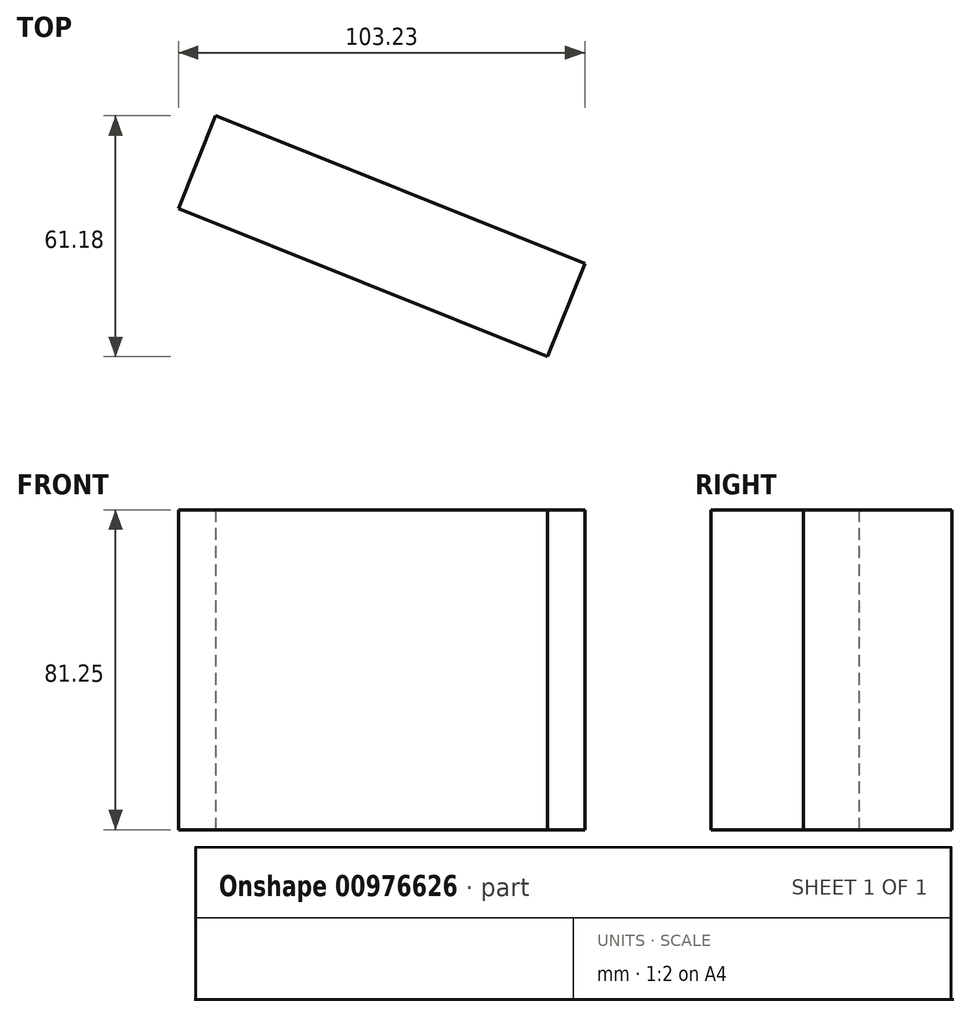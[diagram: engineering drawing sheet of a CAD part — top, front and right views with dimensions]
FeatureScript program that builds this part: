
annotation { "Feature Type Name" : "Feature", "Feature Type Description" : "" }
export const myFeature = defineFeature(function(context is Context, id is Id, definition is map)
    precondition{}
    {
        {
            var Q0;
            Q0=qCreatedBy(makeId("Front.planeOp"),FACE);
            var sketch = newSketch(context, id + "F0", { "sketchPlane" : qUnion([Q0])});
            skLineSegment(sketch, "E0.bottom", {"start": v(-43.63, 37.12) * mm, "end": v(57.4, 37.12) * mm});
            skLineSegment(sketch, "E0.top", {"start": v(-43.63, -44.13) * mm, "end": v(57.4, -44.13) * mm});
            skLineSegment(sketch, "E0.left", {"start": v(-43.63, 37.12) * mm, "end": v(-43.63, -44.13) * mm});
            skLineSegment(sketch, "E0.right", {"start": v(57.4, 37.12) * mm, "end": v(57.4, -44.13) * mm});
            skSolve(sketch);
        }
        {
            var Q0;
            Q0=makeQuery(id+"F0.imprint","IMPRINT",FACE,{"disambiguationData":[TD([[makeQuery(id+"F0.imprint","IMPRINT",EDGE,{"derivedFrom":sQuery(id+"F0.wireOp",EDGE,"E0.bottom")}),-1.0]])]});
            extrude(context, id + "F1", {"entities" : qUnion([Q0]), "depth" : 25.4 * mm, "offsetDistance" : 25.4 * mm});
        }
        {
            var Q0;
            Q0=qCreatedBy(makeId("Front.planeOp"),FACE);
            var sketch = newSketch(context, id + "F2", { "sketchPlane" : qUnion([Q0])});
            skLineSegment(sketch, "E1", {"start": v(-73.26, 0) * mm, "end": v(-73.26, 84.2) * mm});
            skLineSegment(sketch, "E2", {"start": v(-73.26, 0) * mm, "end": v(-20.44, 91.5) * mm});
            skSolve(sketch);
        }
        {
            var Q0;
            Q0=makeQuery(id+"F1.opExtrude","SWEPT_BODY",BODY,{"disambiguationData":[OSD([sQuery(id+"F0.wireOp",EDGE,"E0.bottom"),sQuery(id+"F0.wireOp",EDGE,"E0.top"),sQuery(id+"F0.wireOp",EDGE,"E0.left"),sQuery(id+"F0.wireOp",EDGE,"E0.right")])]});
            var Q1;
            Q1=sQuery(id+"F2.wireOp",EDGE,"E1");
            transform(context, id + "F3", {"entities" : qUnion([Q0]), "transformType" : TransformType.ROTATION, "transformAxis" : qUnion([Q1]), "angle" : 21.85 * degree, "oppositeDirection" : true, "makeCopy" : false});
        }
    });
